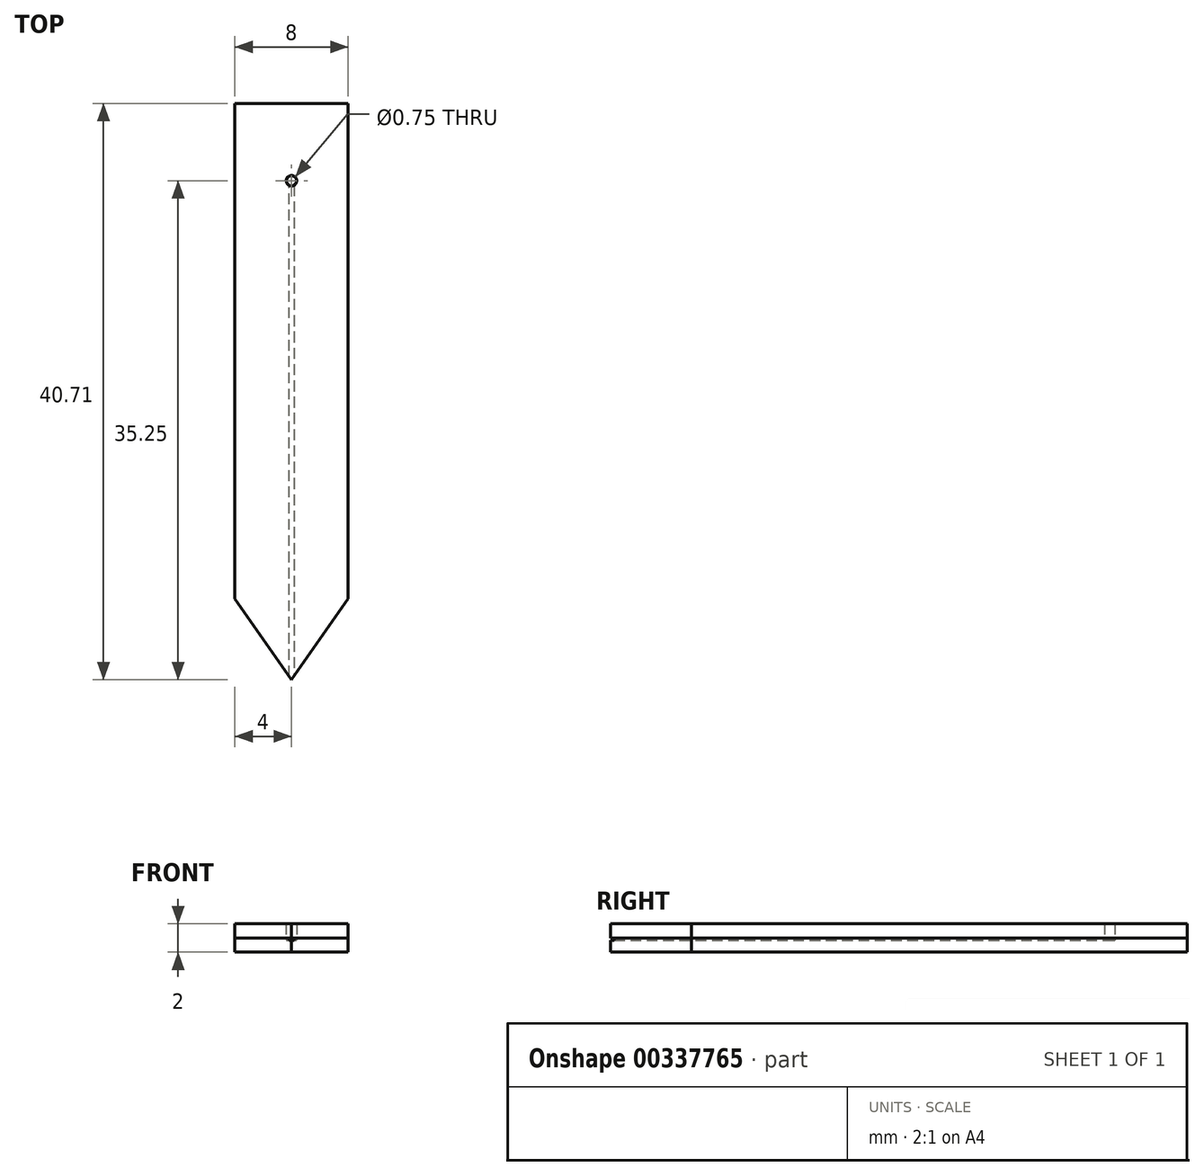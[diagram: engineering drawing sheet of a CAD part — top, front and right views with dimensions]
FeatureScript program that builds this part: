
annotation { "Feature Type Name" : "Feature", "Feature Type Description" : "" }
export const myFeature = defineFeature(function(context is Context, id is Id, definition is map)
    precondition{}
    {
        {
            var Q0;
            Q0=qCreatedBy(makeId("Top.planeOp"),FACE);
            var sketch = newSketch(context, id + "F0", { "sketchPlane" : qUnion([Q0])});
            skLineSegment(sketch, "E0", {"start": v(-4, 5.46) * mm, "end": v(4, 5.46) * mm});
            skLineSegment(sketch, "E1", {"start": v(4, 5.46) * mm, "end": v(4, -29.54) * mm});
            skLineSegment(sketch, "E2", {"start": v(4, -29.54) * mm, "end": v(0, -35.25) * mm});
            skLineSegment(sketch, "E3", {"start": v(0, -35.25) * mm, "end": v(-4, -29.54) * mm});
            skLineSegment(sketch, "E4", {"start": v(-4, -29.54) * mm, "end": v(-4, 5.46) * mm});
            skLineSegment(sketch, "E5", {"start": v(-0.17, -35) * mm, "end": v(-0.18, 0) * mm});
            skLineSegment(sketch, "E6", {"start": v(-0.18, 0) * mm, "end": v(0.18, 0) * mm});
            skLineSegment(sketch, "E7", {"start": v(0.17, 0) * mm, "end": v(0.18, -35) * mm});
            skCircle(sketch, "E8", {"center": v(0, 0) * mm, "radius": 0.35 * mm});
            skSolve(sketch);
        }
        {
            var Q0;
            {var subQ0=sQuery(id+"F0.wireOp",EDGE,"E6");Q0=makeQuery(id+"F0.imprint","IMPRINT",FACE,{"disambiguationData":[TD([[makeQuery(id+"F0.imprint","IMPRINT",EDGE,{"derivedFrom":subQ0}),1.0]])]});}
            var Q1;
            {var subQ1=sQuery(id+"F0.wireOp",EDGE,"E2");var subQ6=sQuery(id+"F0.wireOp",EDGE,"E3");var subQ9=makeQuery(id+"F0.imprint","INTERSECT",VERTEX,{"derivedFrom":[subQ1,subQ6]});Q1=makeQuery(id+"F0.imprint","IMPRINT",FACE,{"disambiguationData":[TD([[makeQuery(id+"F0.imprint","IMPRINT",EDGE,{"disambiguationData":[TD([[subQ9,1.0]])],"derivedFrom":subQ1}),-1.0]])]});}
            var Q2;
            {var subQ0=sQuery(id+"F0.wireOp",EDGE,"E6");Q2=makeQuery(id+"F0.imprint","IMPRINT",FACE,{"disambiguationData":[TD([[makeQuery(id+"F0.imprint","IMPRINT",EDGE,{"derivedFrom":subQ0}),-1.0]])]});}
            extrude(context, id + "F1", {"entities" : qUnion([Q0, Q1, Q2]), "depth" : 0.85 * mm});
        }
        {
            var Q0;
            Q0=makeQuery(id+"F0.imprint","IMPRINT",FACE,{"disambiguationData":[TD([[makeQuery(id+"F0.imprint","IMPRINT",EDGE,{"derivedFrom":sQuery(id+"F0.wireOp",EDGE,"E0")}),-1.0]])]});
            extrude(context, id + "F2", {"entities" : qUnion([Q0]), "operationType" : NewBodyOperationType.ADD, "depth" : 1 * mm});
        }
        {
            var Q0;
            Q0=makeQuery(id+"F2.opExtrude","CAP_FACE",FACE,{"disambiguationData":[OSD([sQuery(id+"F0.wireOp",EDGE,"E0"),sQuery(id+"F0.wireOp",EDGE,"E1"),sQuery(id+"F0.wireOp",EDGE,"E2"),sQuery(id+"F0.wireOp",EDGE,"E3"),sQuery(id+"F0.wireOp",EDGE,"E4"),sQuery(id+"F0.wireOp",EDGE,"E5"),sQuery(id+"F0.wireOp",EDGE,"E7"),sQuery(id+"F0.wireOp",EDGE,"E8")])],"isStart":false});
            var sketch = newSketch(context, id + "F3", { "sketchPlane" : qUnion([Q0])});
            skCircle(sketch, "E9", {"center": v(0, 0) * mm, "radius": 0.37 * mm});
            skLineSegment(sketch, "E10", {"start": v(-4, 5.46) * mm, "end": v(4, 5.46) * mm});
            skLineSegment(sketch, "E11", {"start": v(4, 5.46) * mm, "end": v(4, -29.54) * mm});
            skLineSegment(sketch, "E12", {"start": v(4, -29.54) * mm, "end": v(0.18, -35) * mm});
            skLineSegment(sketch, "E13", {"start": v(0.18, -35) * mm, "end": v(0, -35.25) * mm});
            skLineSegment(sketch, "E14", {"start": v(0, -35.25) * mm, "end": v(-4, -29.54) * mm});
            skLineSegment(sketch, "E15", {"start": v(-4, -29.54) * mm, "end": v(-4, 5.46) * mm});
            skSolve(sketch);
        }
        {
            var Q0;
            Q0=makeQuery(id+"F3.imprint","IMPRINT",FACE,{"disambiguationData":[TD([[makeQuery(id+"F3.imprint","IMPRINT",EDGE,{"derivedFrom":sQuery(id+"F3.wireOp",EDGE,"E10")}),-1.0]])]});
            var Q1;
            {var subQ3=sQuery(id+"F3.wireOp",EDGE,"E13");Q1=makeQuery(id+"F3.imprint","IMPRINT",FACE,{"disambiguationData":[TD([[makeQuery(id+"F3.imprint","IMPRINT",EDGE,{"derivedFrom":subQ3}),-1.0]])]});}
            extrude(context, id + "F4", {"entities" : qUnion([Q0, Q1]), "depth" : 1 * mm});
        }
    });
